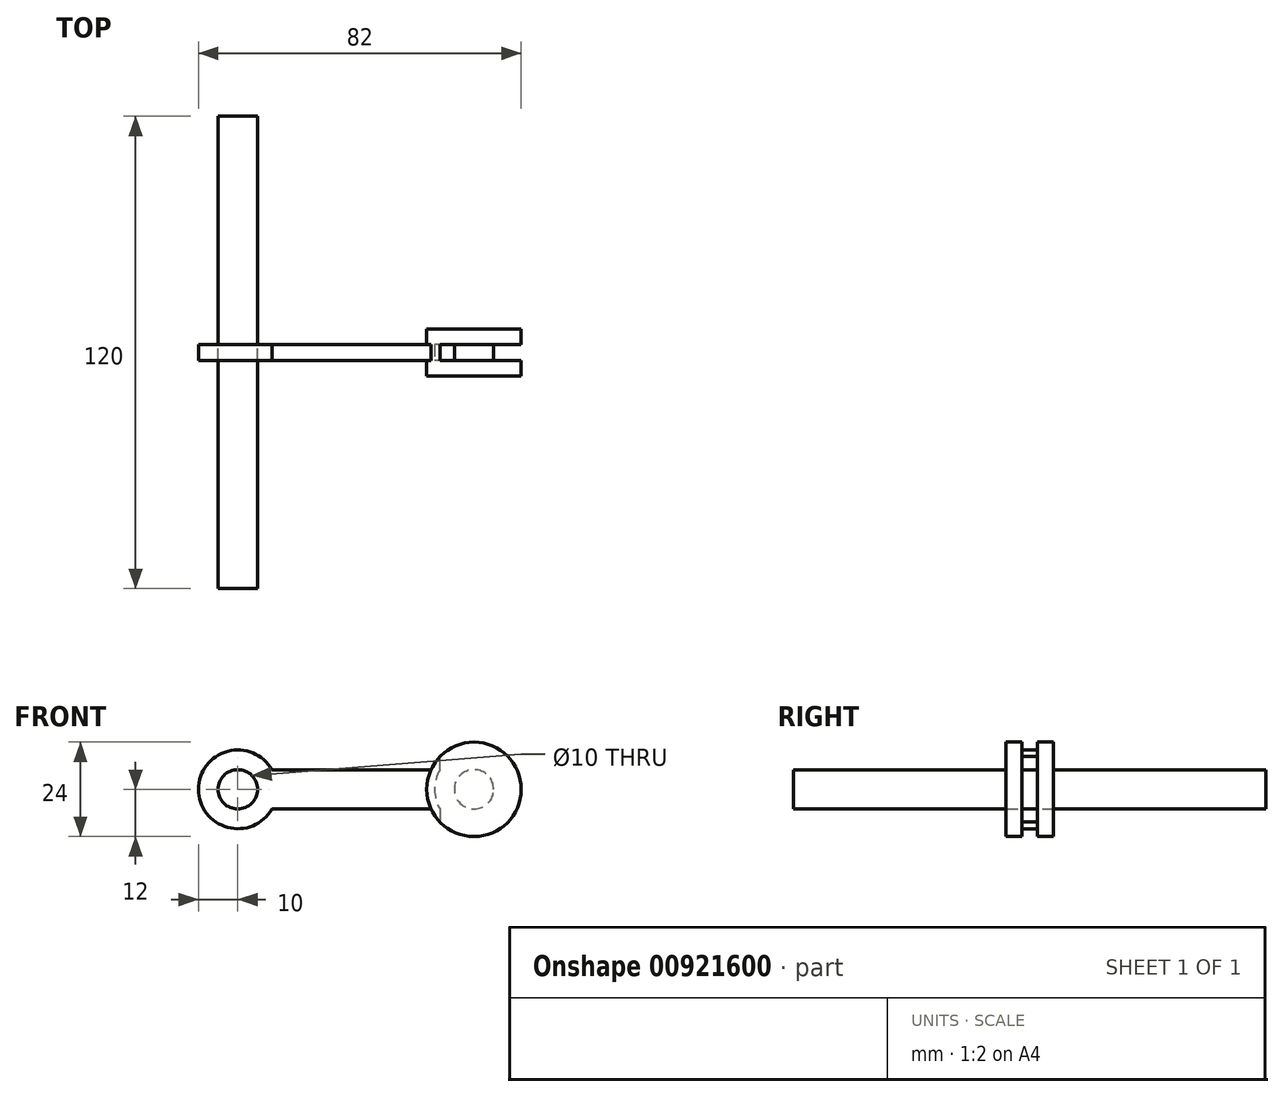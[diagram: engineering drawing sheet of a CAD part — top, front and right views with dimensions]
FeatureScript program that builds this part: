
annotation { "Feature Type Name" : "Feature", "Feature Type Description" : "" }
export const myFeature = defineFeature(function(context is Context, id is Id, definition is map)
    precondition{}
    {
        {
            var Q0;
            Q0=qCreatedBy(makeId("Front.planeOp"),FACE);
            var sketch = newSketch(context, id + "F0", { "sketchPlane" : qUnion([Q0])});
            skCircle(sketch, "E0", {"center": v(0, 0) * mm, "radius": 5 * mm});
            skSolve(sketch);
        }
        {
            var Q0;
            Q0 = qSketchRegion(id + "F0", true);
            extrude(context, id + "F1", {"entities" : qUnion([Q0]), "endBound" : BoundingType.SYMMETRIC, "depth" : 120 * mm, "offsetDistance" : 25 * mm});
        }
        {
            var Q0;
            Q0=qCreatedBy(makeId("Front.planeOp"),FACE);
            var sketch = newSketch(context, id + "F2", { "sketchPlane" : qUnion([Q0])});
            skCircle(sketch, "E1.0", {"center": v(0, 0) * mm, "radius": 5 * mm});
            skCircle(sketch, "E2", {"center": v(0, 0) * mm, "radius": 10 * mm});
            skCircle(sketch, "E3", {"center": v(60, 0) * mm, "radius": 12 * mm});
            skLineSegment(sketch, "E4", {"start": v(8.66, 5) * mm, "end": v(49.1, 5) * mm});
            skLineSegment(sketch, "E5.MirrorCS", {"start": v(8.66, -5) * mm, "end": v(49.1, -5) * mm});
            skSolve(sketch);
        }
        {
            var Q0;
            Q0 = qSketchRegion(id + "F2", true);
            extrude(context, id + "F3", {"entities" : qUnion([Q0]), "endBound" : BoundingType.SYMMETRIC, "depth" : 4 * mm, "offsetDistance" : 25 * mm});
        }
        {
            var Q0;
            Q0=qCreatedBy(makeId("Front.planeOp"),FACE);
            var sketch = newSketch(context, id + "F4", { "sketchPlane" : qUnion([Q0])});
            skCircle(sketch, "E6", {"center": v(60, 0) * mm, "radius": 12 * mm});
            skSolve(sketch);
        }
        {
            var Q0;
            Q0 = qSketchRegion(id + "F4", true);
            extrude(context, id + "F5", {"entities" : qUnion([Q0]), "operationType" : NewBodyOperationType.ADD, "endBound" : BoundingType.SYMMETRIC, "depth" : 12 * mm, "offsetDistance" : 25 * mm});
        }
        {
            var Q0;
            Q0=qCreatedBy(makeId("Front.planeOp"),FACE);
            var sketch = newSketch(context, id + "F6", { "sketchPlane" : qUnion([Q0])});
            skCircle(sketch, "E7", {"center": v(60, 0) * mm, "radius": 5 * mm});
            skArc(sketch, "E8.0", {"start": v(51.34, -8.3) * mm, "mid": v(72, 0) * mm, "end": v(51.34, 8.3) * mm});
            skArc(sketch, "E9", {"start": v(51.34, 5) * mm, "mid": v(50, 0) * mm, "end": v(51.34, -5) * mm});
            skLineSegment(sketch, "E10", {"start": v(51.34, 5) * mm, "end": v(51.34, 8.3) * mm});
            skLineSegment(sketch, "E11", {"start": v(51.34, -5) * mm, "end": v(51.34, -8.3) * mm});
            skSolve(sketch);
        }
        {
            var Q0;
            Q0 = qSketchRegion(id + "F6", true);
            extrude(context, id + "F7", {"entities" : qUnion([Q0]), "operationType" : NewBodyOperationType.REMOVE, "endBound" : BoundingType.SYMMETRIC, "oppositeDirection" : true, "depth" : 4 * mm, "offsetDistance" : 25 * mm});
        }
    });
